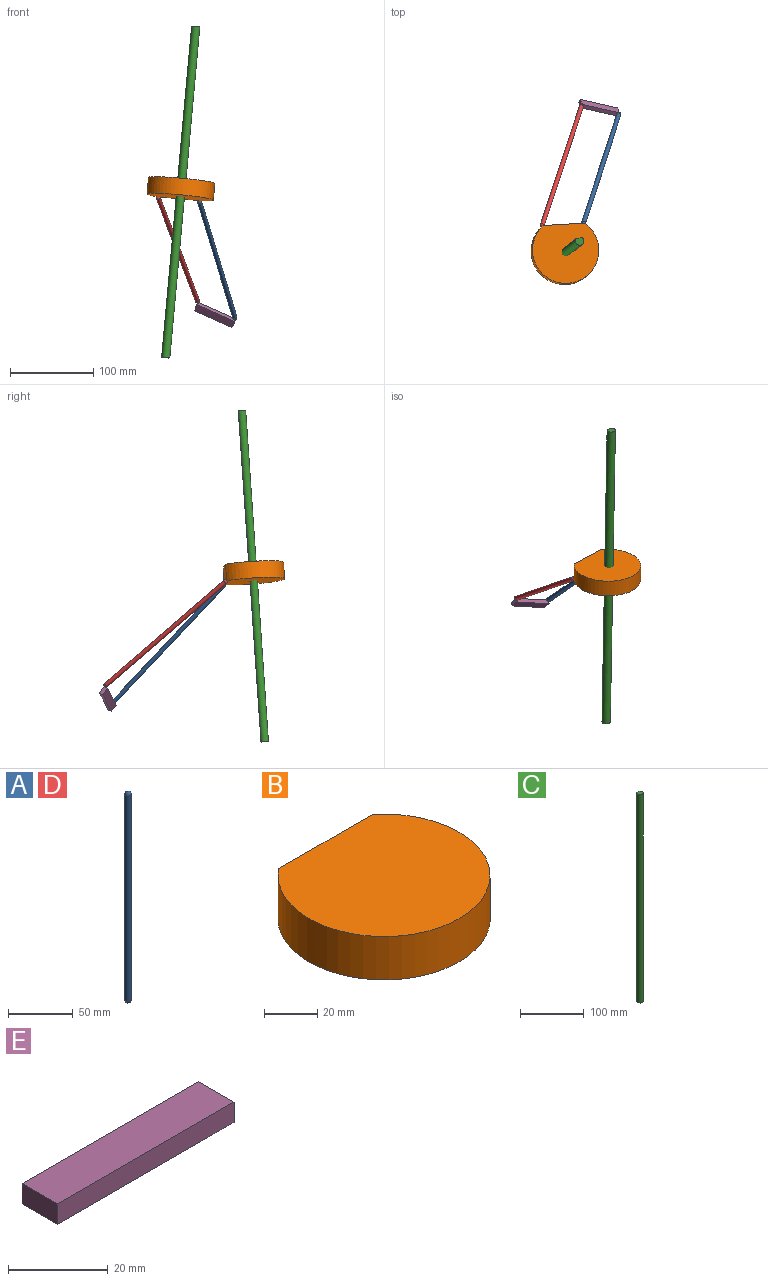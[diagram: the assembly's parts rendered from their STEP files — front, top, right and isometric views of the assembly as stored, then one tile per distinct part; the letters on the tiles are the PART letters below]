
ASSEMBLY  parts=5 mates=5
PART A: 3 faces, bbox 5x5x200 mm
  f0: cylinder r=2.5mm len=195mm, axis (0,0,-1), area 3063.1mm2, adj f1,f2
  f1: sphere r=2.5mm, area 39.3mm2, adj f0
  f2: sphere r=2.5mm, area 39.3mm2, adj f0
PART B: 4 faces, bbox 80x71.2x20 mm
  f0: plane 50x20mm, normal (0,1,0), area 1000mm2, adj f1,f2,f3
  f1: cylinder r=40mm len=80mm, axis (0,0,-1), area 3946.3mm2, adj f0,f2,f3
  f2: plane 80x71.23mm, normal (0,0,1), area 4727mm2, adj f0,f1
  f3: plane 80x71.23mm, normal (0,0,-1), area 4727mm2, adj f0,f1
PART C: 4 faces, bbox 10x8.8x400 mm
  f0: plane 400x6.4mm, normal (0,1,0), area 2561.1mm2, adj f1,f2,f3
  f1: cylinder r=5mm len=400mm, axis (0,0,-1), area 9787mm2, adj f0,f2,f3
  f2: plane 10x8.84mm, normal (0,0,1), area 73.5mm2, adj f0,f1
  f3: plane 10x8.84mm, normal (0,0,-1), area 73.5mm2, adj f0,f1
PART D: same geometry as A
PART E: 6 faces, bbox 50x10x5 mm
  f0: plane 10x5mm, normal (-1,0,0), area 50mm2, adj f1,f3,f4,f5
  f1: plane 50x5mm, normal (0,-1,0), area 250mm2, adj f0,f2,f4,f5
  f2: plane 10x5mm, normal (1,0,0), area 50mm2, adj f1,f3,f4,f5
  f3: plane 50x5mm, normal (0,1,0), area 250mm2, adj f0,f2,f4,f5
  f4: plane 50x10mm, normal (0,0,1), area 500mm2, adj f0,f1,f2,f3
  f5: plane 50x10mm, normal (0,0,-1), area 500mm2, adj f0,f1,f2,f3
PLACE A rot(axis=(0.7,-0.46,0.54),53.8deg) t=(408.23,321.65,403.73)mm
PLACE B rot(axis=(-0.51,0.72,0.47),7.4deg) t=(53.36,24.26,338.53)mm
PLACE C rot(axis=(-0.51,0.72,0.47),7.4deg) t=(36.05,8.81,145.83)mm fixed
PLACE D rot(axis=(0.71,-0.49,0.51),59.6deg) t=(348.77,316.42,450.52)mm
PLACE E rot(axis=(-0.89,0.46,0),60.3deg) t=(105.01,163.93,235.61)mm
MATE ball D.f0 <-> E.f4  axis (-0.24,-0.73,0.63) through (74.9,200.82,212.12)mm
MATE ball B.f3 <-> A.f0  axis (0.09,0.07,0.99) through (76.22,56.81,334.23)mm
MATE ball A.f0 <-> E.f4  axis (-0.22,-0.67,0.71) through (119.62,190.72,192.15)mm
MATE ball D.f0 <-> B.f3  axis (-0.24,-0.73,0.63) through (26.53,53.92,338.92)mm
MATE slider B.f2 <-> C.f1  axis (0.09,0.07,0.99) through (55.3,23.43,358.54)mm
